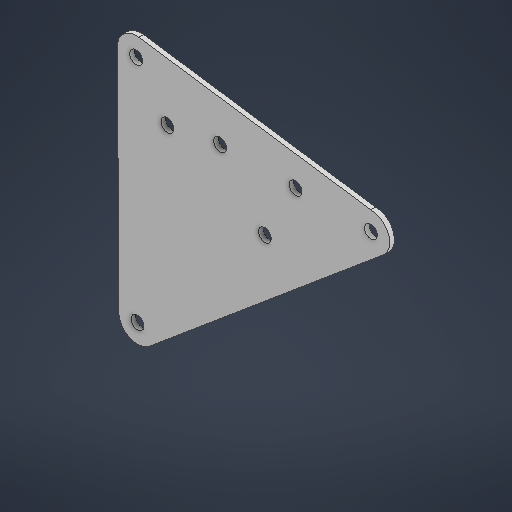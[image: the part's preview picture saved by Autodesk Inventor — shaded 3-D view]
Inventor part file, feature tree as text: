
AUTODESK INVENTOR PART (.ipt)
format: ipt  version: 2025.2 (Build 292293000, 293)  size: 197,120 bytes
history: native  units: in
note: dims shown in document units (in); Inventor stores cm internally (conversion verified against a paired STEP export)
features: extrude x1, sketch x1
ambient origin geometry x8: Origin, YZ Plane, XZ Plane, XY Plane, X Axis, Y Axis, Z Axis, Center Point
bodies: Solid1 (feature_tree)
feature tree (2):
  extrude  "Extrusion1"  Depth=0.0625in TaperAngle=0.0deg
  sketch  "Sketch1"  dims[d0=0.5in d1=0.5in d2=0.5in d3=0.5in d4=0.5in d5=0.5in d6=0.5in d7=0.0625in d8=0.0in]
